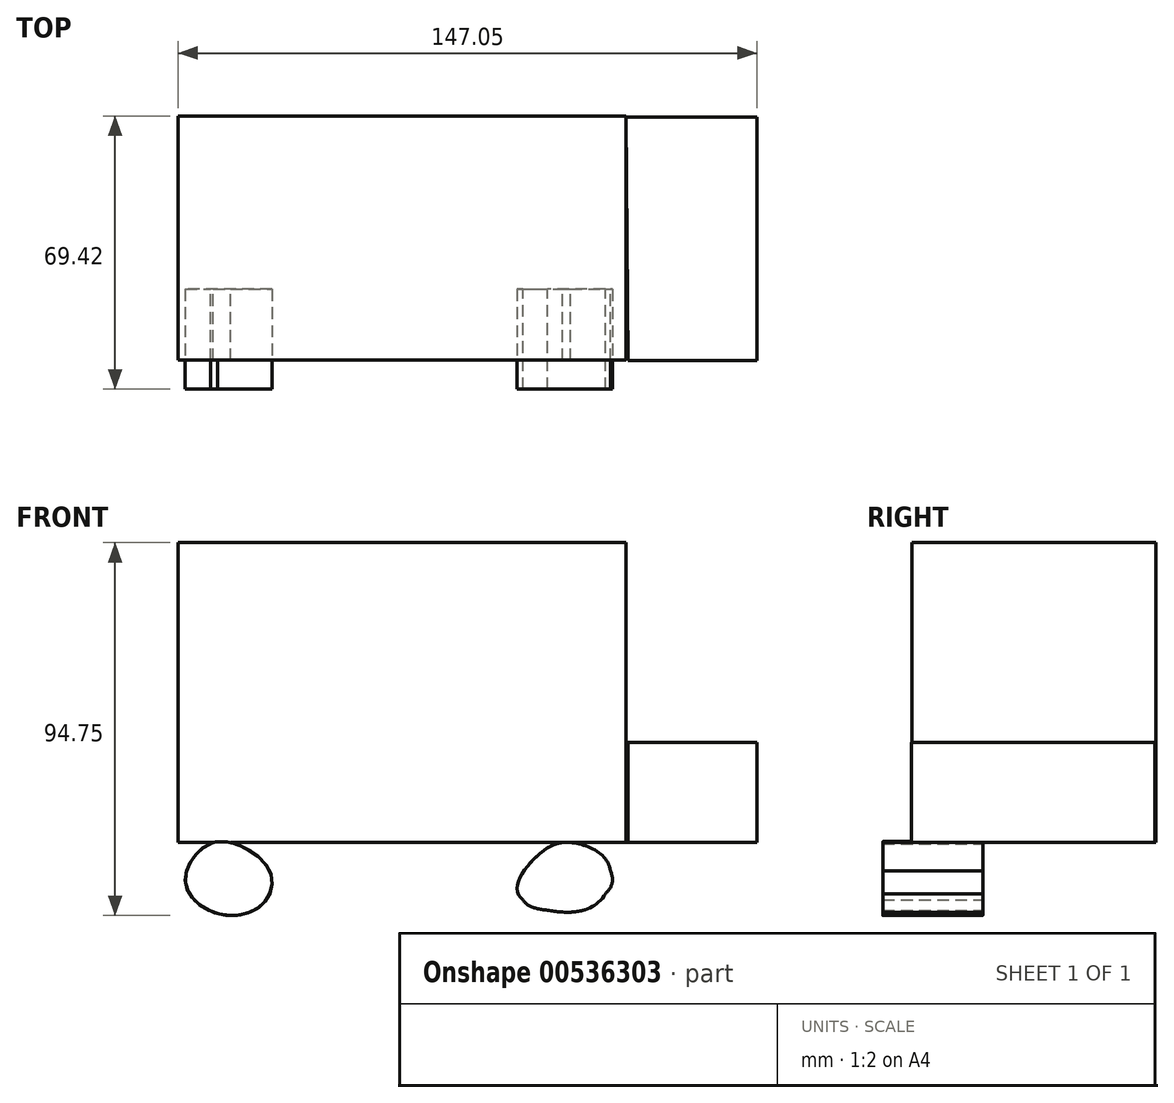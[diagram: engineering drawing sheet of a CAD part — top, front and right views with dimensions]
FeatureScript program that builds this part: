
annotation { "Feature Type Name" : "Feature", "Feature Type Description" : "" }
export const myFeature = defineFeature(function(context is Context, id is Id, definition is map)
    precondition{}
    {
        {
            var Q0;
            Q0=qCreatedBy(makeId("Top.planeOp"),FACE);
            var sketch = newSketch(context, id + "F0", { "sketchPlane" : qUnion([Q0])});
            skLineSegment(sketch, "E0", {"start": v(-70.76, 44.02) * mm, "end": v(38.56, 44.02) * mm});
            skLineSegment(sketch, "E1", {"start": v(-52.83, -18.02) * mm, "end": v(42.98, -18.02) * mm});
            skLineSegment(sketch, "E2", {"start": v(-52.83, -18.02) * mm, "end": v(-63.97, -18.02) * mm});
            skLineSegment(sketch, "E3", {"start": v(-63.97, -18.02) * mm, "end": v(-70.76, -18.02) * mm});
            skLineSegment(sketch, "E4", {"start": v(-70.76, -18.02) * mm, "end": v(-70.76, 44.02) * mm});
            skLineSegment(sketch, "E5", {"start": v(38.56, 44.02) * mm, "end": v(42.98, 44.02) * mm});
            skLineSegment(sketch, "E6", {"start": v(42.98, 44.02) * mm, "end": v(42.98, -20) * mm});
            skSolve(sketch);
        }
        {
            var Q0;
            Q0=makeQuery(id+"F0.imprint","IMPRINT",FACE,{"disambiguationData":[TD([[makeQuery(id+"F0.imprint","IMPRINT",EDGE,{"derivedFrom":sQuery(id+"F0.wireOp",EDGE,"E0")}),-1.0]])]});
            extrude(context, id + "F1", {"entities" : qUnion([Q0]), "depth" : 76.2 * mm, "offsetDistance" : 25.4 * mm});
        }
        {
            var Q0;
            Q0=qCreatedBy(makeId("Top.planeOp"),FACE);
            var sketch = newSketch(context, id + "F2", { "sketchPlane" : qUnion([Q0])});
            skLineSegment(sketch, "E7", {"start": v(43.5, -18.14) * mm, "end": v(76.29, -18.14) * mm});
            skLineSegment(sketch, "E8", {"start": v(76.29, -18.14) * mm, "end": v(76.29, 43.73) * mm});
            skLineSegment(sketch, "E9", {"start": v(43.03, 43.73) * mm, "end": v(76.29, 43.73) * mm});
            skLineSegment(sketch, "E10", {"start": v(43.5, -18.14) * mm, "end": v(43.03, 43.73) * mm});
            skSolve(sketch);
        }
        {
            var Q0;
            Q0=makeQuery(id+"F2.imprint","IMPRINT",FACE,{"disambiguationData":[TD([[makeQuery(id+"F2.imprint","IMPRINT",EDGE,{"derivedFrom":sQuery(id+"F2.wireOp",EDGE,"E7")}),1.0]])]});
            extrude(context, id + "F3", {"entities" : qUnion([Q0]), "depth" : 25.4 * mm, "offsetDistance" : 25.4 * mm});
        }
        {
            var Q0;
            Q0=qCreatedBy(makeId("Front.planeOp"),FACE);
            var sketch = newSketch(context, id + "F4", { "sketchPlane" : qUnion([Q0])});
            skFitSpline(sketch, "E11", {"points": [v(-61.82, 0) * mm, v(-67.17, -6.75) * mm, v(-65.55, -15.12) * mm, v(-54.38, -17.44) * mm, v(-47.4, -11.4) * mm, v(-52.06, -3.26) * mm, v(-61.82, 0) * mm]});
            skFitSpline(sketch, "E12", {"points": [v(27.49, 0) * mm, v(17.02, -7.21) * mm, v(21.44, -17.68) * mm, v(36.1, -16.05) * mm, v(38.89, -7.68) * mm, v(27.49, 0) * mm]});
            skSolve(sketch);
        }
        {
            var Q0;
            Q0=makeQuery(id+"F4.imprint","IMPRINT",FACE,{"disambiguationData":[TD([[makeQuery(id+"F4.imprint","IMPRINT",EDGE,{"derivedFrom":sQuery(id+"F4.wireOp",EDGE,"E11")}),1.0]])]});
            extrude(context, id + "F5", {"entities" : qUnion([Q0]), "operationType" : NewBodyOperationType.ADD, "depth" : 25.4 * mm, "offsetDistance" : 25.4 * mm});
        }
        {
            var Q0;
            Q0=qCreatedBy(makeId("Front.planeOp"),FACE);
            var sketch = newSketch(context, id + "F6", { "sketchPlane" : qUnion([Q0])});
            skFitSpline(sketch, "E13", {"points": [v(28.89, 0) * mm, v(17.95, -6.98) * mm, v(17.26, -15.12) * mm, v(31.21, -16.28) * mm, v(39.58, -9.07) * mm, v(28.89, 0) * mm]});
            skSolve(sketch);
        }
        {
            var Q0;
            Q0=makeQuery(id+"F6.imprint","IMPRINT",FACE,{"disambiguationData":[TD([[makeQuery(id+"F6.imprint","IMPRINT",EDGE,{"derivedFrom":sQuery(id+"F6.wireOp",EDGE,"E13")}),1.0]])]});
            extrude(context, id + "F7", {"entities" : qUnion([Q0]), "operationType" : NewBodyOperationType.ADD, "depth" : 25.4 * mm, "offsetDistance" : 25.4 * mm});
        }
        {
            var Q0;
            Q0=qCreatedBy(makeId("Front.planeOp"),FACE);
            var sketch = newSketch(context, id + "F8", { "sketchPlane" : qUnion([Q0])});
            skFitSpline(sketch, "E14", {"points": [v(28.89, 0) * mm, v(38.42, -5.12) * mm, v(36.33, -14.89) * mm, v(24.7, -17.44) * mm, v(15.4, -12.33) * mm, v(21.44, -2.56) * mm, v(28.89, 0) * mm]});
            skSolve(sketch);
        }
        {
            var Q0;
            Q0=makeQuery(id+"F8.imprint","IMPRINT",FACE,{"disambiguationData":[TD([[makeQuery(id+"F8.imprint","IMPRINT",EDGE,{"derivedFrom":sQuery(id+"F8.wireOp",EDGE,"E14")}),-1.0]])]});
            extrude(context, id + "F9", {"entities" : qUnion([Q0]), "operationType" : NewBodyOperationType.ADD, "depth" : 25.4 * mm, "offsetDistance" : 25.4 * mm});
        }
        {
            var Q0;
            Q0=qCreatedBy(makeId("Front.planeOp"),FACE);
            var sketch = newSketch(context, id + "F10", { "sketchPlane" : qUnion([Q0])});
            skFitSpline(sketch, "E15", {"points": [v(-57.4, 0) * mm, v(-47.4, -7.44) * mm, v(-49.5, -15.82) * mm, v(-60.43, -18.14) * mm, v(-68.8, -10.7) * mm, v(-65.08, -1.86) * mm, v(-57.4, 0) * mm]});
            skSolve(sketch);
        }
        {
            var Q0;
            Q0=makeQuery(id+"F10.imprint","IMPRINT",FACE,{"disambiguationData":[TD([[makeQuery(id+"F10.imprint","IMPRINT",EDGE,{"derivedFrom":sQuery(id+"F10.wireOp",EDGE,"E15")}),-1.0]])]});
            extrude(context, id + "F11", {"entities" : qUnion([Q0]), "operationType" : NewBodyOperationType.ADD, "depth" : 25.4 * mm, "offsetDistance" : 25.4 * mm});
        }
    });
